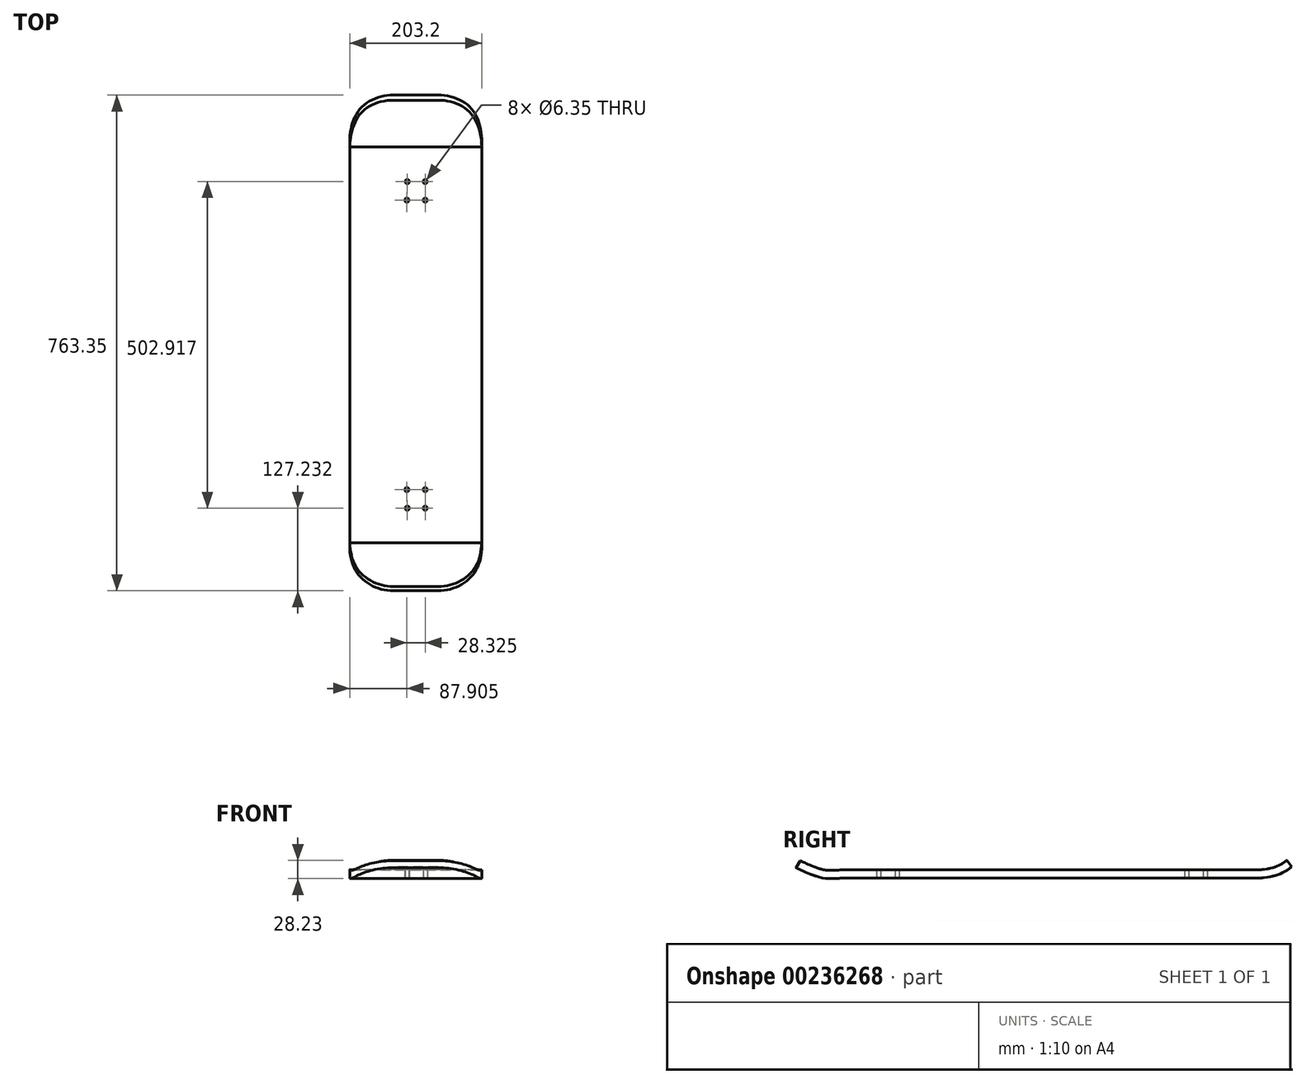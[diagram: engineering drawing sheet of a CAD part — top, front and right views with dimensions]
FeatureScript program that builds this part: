
annotation { "Feature Type Name" : "Feature", "Feature Type Description" : "" }
export const myFeature = defineFeature(function(context is Context, id is Id, definition is map)
    precondition{}
    {
        {
            var Q0;
            Q0=qCreatedBy(makeId("Top.planeOp"),FACE);
            var sketch = newSketch(context, id + "F0", { "sketchPlane" : qUnion([Q0])});
            skLineSegment(sketch, "E0.bottom", {"start": v(101.6, -304.8) * mm, "end": v(-101.6, -304.8) * mm});
            skLineSegment(sketch, "E0.top", {"start": v(101.6, 304.8) * mm, "end": v(-101.6, 304.8) * mm});
            skLineSegment(sketch, "E0.left", {"start": v(101.6, -304.8) * mm, "end": v(101.6, 304.8) * mm});
            skLineSegment(sketch, "E0.right", {"start": v(-101.6, -304.8) * mm, "end": v(-101.6, 304.8) * mm});
            skPoint(sketch, "E0.middle", {"position": v(0, 0) * mm});
            skPoint(sketch, "E1.middle", {"position": v(0, 235.58) * mm});
            skCircle(sketch, "E2", {"center": v(-13.08, 251.46) * mm, "radius": 3.18 * mm});
            skCircle(sketch, "E3", {"center": v(14.63, 251.46) * mm, "radius": 3.18 * mm});
            skCircle(sketch, "E4", {"center": v(-13.7, 222.88) * mm, "radius": 3.18 * mm});
            skCircle(sketch, "E5", {"center": v(14.63, 222.88) * mm, "radius": 3.18 * mm});
            skPoint(sketch, "E1.left.end.orphan", {"position": v(25.4, 260.98) * mm});
            skPoint(sketch, "E1.right.end.orphan", {"position": v(-25.4, 260.98) * mm});
            skPoint(sketch, "E1.bottom.end.orphan", {"position": v(-25.4, 210.18) * mm});
            skPoint(sketch, "E1.bottom.start.orphan", {"position": v(25.4, 210.18) * mm});
            skCircle(sketch, "E6.MirrorC", {"center": v(14.63, -222.88) * mm, "radius": 3.18 * mm});
            skCircle(sketch, "E7.MirrorC", {"center": v(-13.7, -222.88) * mm, "radius": 3.18 * mm});
            skCircle(sketch, "E8.MirrorC", {"center": v(-13.08, -251.46) * mm, "radius": 3.18 * mm});
            skCircle(sketch, "E9.MirrorC", {"center": v(14.63, -251.46) * mm, "radius": 3.18 * mm});
            skSolve(sketch);
        }
        {
            var Q0;
            Q0 = qSketchRegion(id + "F0", true);
            extrude(context, id + "F1", {"entities" : qUnion([Q0]), "endBound" : BoundingType.SYMMETRIC, "depth" : 12.7 * mm});
        }
        {
            var Q0;
            Q0=qCreatedBy(makeId("Right.planeOp"),FACE);
            var sketch = newSketch(context, id + "F2", { "sketchPlane" : qUnion([Q0])});
            skFitSpline(sketch, "E10", {"points": [v(305.22, 0) * mm, v(337.82, 0) * mm, v(364.5, 5.93) * mm, v(381.08, 16) * mm], "startDerivative": vector(88.64, -3.52) * mm, "endDerivative": vector(53.31, 38.4) * mm});
            skFitSpline(sketch, "E11", {"points": [v(-306.42, 0) * mm, v(-336.45, 0) * mm, v(-363.6, 9.27) * mm, v(-376.83, 15.5) * mm], "startDerivative": vector(-80.1, -7.04) * mm, "endDerivative": vector(-45.76, 22.16) * mm});
            skSolve(sketch);
        }
        {
            var Q0;
            Q0=makeQuery(id+"F1.opExtrude","SWEPT_FACE",FACE,{"disambiguationData":[OSD([sQuery(id+"F0.wireOp",EDGE,"E0.top")])]});
            var Q1;
            Q1=sQuery(id+"F2.wireOp",EDGE,"E10");
            sweep(context, id + "F3", {"operationType" : NewBodyOperationType.ADD, "profiles" : qUnion([Q0]), "path" : qUnion([Q1])});
        }
        {
            var Q0;
            Q0=makeQuery(id+"F1.opExtrude","SWEPT_FACE",FACE,{"disambiguationData":[OSD([sQuery(id+"F0.wireOp",EDGE,"E0.bottom")])]});
            var Q1;
            Q1=sQuery(id+"F2.wireOp",EDGE,"E11");
            sweep(context, id + "F4", {"operationType" : NewBodyOperationType.ADD, "profiles" : qUnion([Q0]), "path" : qUnion([Q1])});
        }
        {
            var Q0;
            Q0=makeQuery(id+"F3.opSweep","CAP_EDGE",EDGE,{"disambiguationData":[OSD([sQuery(id+"F0.wireOp",EDGE,"E0.top"),sQuery(id+"F0.wireOp",EDGE,"E0.left"),sQuery(id+"F2.wireOp",VERTEX,"E10.end")])],"isStart":false});
            var Q1;
            Q1=makeQuery(id+"F3.opSweep","CAP_EDGE",EDGE,{"disambiguationData":[OSD([sQuery(id+"F0.wireOp",EDGE,"E0.top"),sQuery(id+"F0.wireOp",EDGE,"E0.right"),sQuery(id+"F2.wireOp",VERTEX,"E10.end")])],"isStart":false});
            var Q2;
            Q2=makeQuery(id+"F4.opSweep","CAP_EDGE",EDGE,{"disambiguationData":[OSD([sQuery(id+"F0.wireOp",EDGE,"E0.bottom"),sQuery(id+"F0.wireOp",EDGE,"E0.right"),sQuery(id+"F2.wireOp",VERTEX,"E11.end")])],"isStart":false});
            var Q3;
            Q3=makeQuery(id+"F4.opSweep","CAP_EDGE",EDGE,{"disambiguationData":[OSD([sQuery(id+"F0.wireOp",EDGE,"E0.bottom"),sQuery(id+"F0.wireOp",EDGE,"E0.left"),sQuery(id+"F2.wireOp",VERTEX,"E11.end")])],"isStart":false});
            fillet(context, id + "F5", {"entities" : qUnion([Q0, Q1, Q2, Q3]), "radius" : 67.45 * mm, "tangentPropagation" : true, "allowEdgeOverflow" : false});
        }
    });
